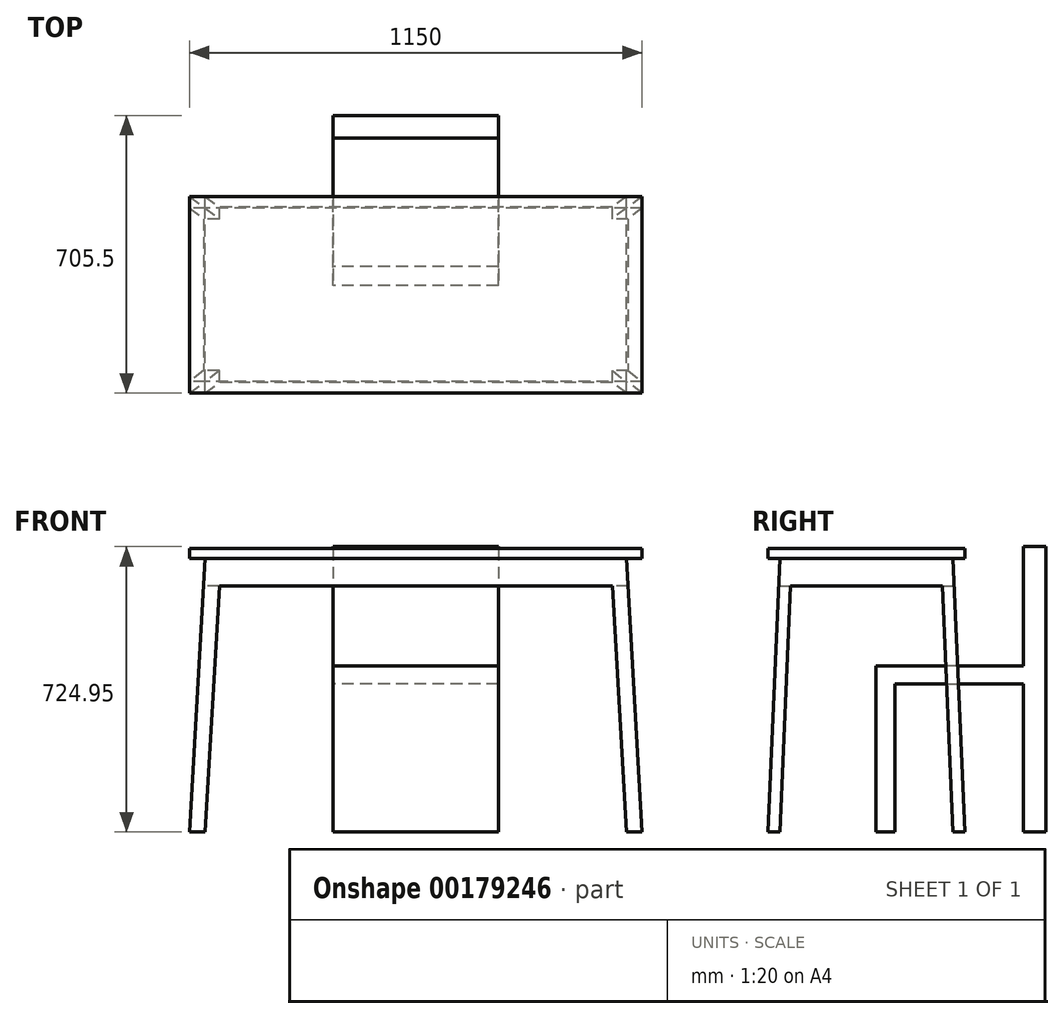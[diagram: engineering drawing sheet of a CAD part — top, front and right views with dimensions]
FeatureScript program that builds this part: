
annotation { "Feature Type Name" : "Feature", "Feature Type Description" : "" }
export const myFeature = defineFeature(function(context is Context, id is Id, definition is map)
    precondition{}
    {
        {
            var Q0;
            Q0=qCreatedBy(makeId("Front.planeOp"),FACE);
            var sketch = newSketch(context, id + "F0", { "sketchPlane" : qUnion([Q0])});
            skLineSegment(sketch, "E0.bottom", {"start": v(-575, 0) * mm, "end": v(575, 0) * mm});
            skLineSegment(sketch, "E0.top", {"start": v(-575, 720) * mm, "end": v(575, 720) * mm});
            skLineSegment(sketch, "E0.left", {"start": v(-575, 0) * mm, "end": v(-575, 720) * mm});
            skLineSegment(sketch, "E0.right", {"start": v(575, 0) * mm, "end": v(575, 720) * mm});
            skSolve(sketch);
        }
        {
            var Q0;
            Q0 = qSketchRegion(id + "F0", true);
            extrude(context, id + "F1", {"entities" : qUnion([Q0]), "depth" : 500 * mm});
        }
        {
            var Q0;
            Q0=makeQuery(id+"F1.opExtrude","CAP_FACE",FACE,{"disambiguationData":[OSD([sQuery(id+"F0.wireOp",EDGE,"E0.bottom"),sQuery(id+"F0.wireOp",EDGE,"E0.top"),sQuery(id+"F0.wireOp",EDGE,"E0.left"),sQuery(id+"F0.wireOp",EDGE,"E0.right")])],"isStart":true});
            var sketch = newSketch(context, id + "F2", { "sketchPlane" : qUnion([Q0])});
            skLineSegment(sketch, "E1", {"start": v(-575, 0) * mm, "end": v(-535, 695) * mm});
            skLineSegment(sketch, "E2", {"start": v(-535, 695) * mm, "end": v(-575, 695) * mm});
            skLineSegment(sketch, "E3", {"start": v(-575, 695) * mm, "end": v(-617.04, 718.64) * mm});
            skLineSegment(sketch, "E4", {"start": v(-617.04, 718.64) * mm, "end": v(-617.04, 757.2) * mm});
            skLineSegment(sketch, "E5", {"start": v(-617.04, 757.2) * mm, "end": v(680.07, 757.2) * mm});
            skLineSegment(sketch, "E6", {"start": v(680.07, 757.2) * mm, "end": v(680.07, 727.9) * mm});
            skLineSegment(sketch, "E7", {"start": v(535, 695) * mm, "end": v(663.8, 695) * mm});
            skLineSegment(sketch, "E8", {"start": v(663.8, 695) * mm, "end": v(680.07, 727.9) * mm});
            skLineSegment(sketch, "E9", {"start": v(575, 0) * mm, "end": v(535, 695) * mm});
            skLineSegment(sketch, "E10", {"start": v(-575, 0) * mm, "end": v(-534.93, 0) * mm});
            skLineSegment(sketch, "E11", {"start": v(-498.96, 625) * mm, "end": v(498.96, 625) * mm});
            skLineSegment(sketch, "E12", {"start": v(534.93, 0) * mm, "end": v(498.96, 625) * mm});
            skLineSegment(sketch, "E13", {"start": v(-534.93, 0) * mm, "end": v(-498.96, 625) * mm});
            skLineSegment(sketch, "E14", {"start": v(534.93, 0) * mm, "end": v(575, 0) * mm});
            skSolve(sketch);
        }
        {
            var Q0;
            {var subQ1=sQuery(id+"F2.wireOp",EDGE,"E3");Q0=makeQuery(id+"F2.imprint","IMPRINT",FACE,{"disambiguationData":[TD([[makeQuery(id+"F2.imprint","IMPRINT",EDGE,{"derivedFrom":subQ1}),-1.0]])]});}
            var Q1;
            {var subQ0=sQuery(id+"F2.wireOp",EDGE,"E1");Q1=makeQuery(id+"F2.imprint","IMPRINT",FACE,{"disambiguationData":[TD([[makeQuery(id+"F2.imprint","IMPRINT",EDGE,{"derivedFrom":subQ0}),1.0]])]});}
            var Q2;
            Q2=makeQuery(id+"F2.imprint","IMPRINT",FACE,{"disambiguationData":[TD([[makeQuery(id+"F2.imprint","IMPRINT",EDGE,{"derivedFrom":sQuery(id+"F2.wireOp",EDGE,"E11")}),-1.0]])]});
            var Q3;
            {var subQ0=sQuery(id+"F2.wireOp",EDGE,"E9");Q3=makeQuery(id+"F2.imprint","IMPRINT",FACE,{"disambiguationData":[TD([[makeQuery(id+"F2.imprint","IMPRINT",EDGE,{"derivedFrom":subQ0}),-1.0]])]});}
            extrude(context, id + "F3", {"entities" : qUnion([Q0, Q1, Q2, Q3]), "operationType" : NewBodyOperationType.REMOVE, "endBound" : BoundingType.THROUGH_ALL, "oppositeDirection" : true, "depth" : 25 * mm});
        }
        {
            var Q0;
            Q0=makeQuery(id+"F1.opExtrude","SWEPT_FACE",FACE,{"disambiguationData":[OSD([sQuery(id+"F0.wireOp",EDGE,"E0.left")])]});
            var sketch = newSketch(context, id + "F4", { "sketchPlane" : qUnion([Q0])});
            skLineSegment(sketch, "E15", {"start": v(0, 0) * mm, "end": v(30, 695) * mm});
            skLineSegment(sketch, "E16", {"start": v(30, 695) * mm, "end": v(-66.16, 695) * mm});
            skLineSegment(sketch, "E17", {"start": v(-66.16, 695) * mm, "end": v(0, 0) * mm});
            skLineSegment(sketch, "E18", {"start": v(500, 0) * mm, "end": v(470, 695) * mm});
            skLineSegment(sketch, "E19", {"start": v(470, 695) * mm, "end": v(521.08, 695) * mm});
            skLineSegment(sketch, "E20", {"start": v(521.08, 695) * mm, "end": v(500, 0) * mm});
            skLineSegment(sketch, "E21", {"start": v(30.03, 0) * mm, "end": v(57, 625) * mm});
            skLineSegment(sketch, "E22", {"start": v(57, 625) * mm, "end": v(443, 625) * mm});
            skLineSegment(sketch, "E23", {"start": v(443, 625) * mm, "end": v(469.97, 0) * mm});
            skLineSegment(sketch, "E24", {"start": v(30.03, 0) * mm, "end": v(469.97, 0) * mm});
            skSolve(sketch);
        }
        {
            var Q0;
            Q0 = qSketchRegion(id + "F4", true);
            extrude(context, id + "F5", {"entities" : qUnion([Q0]), "operationType" : NewBodyOperationType.REMOVE, "endBound" : BoundingType.THROUGH_ALL, "oppositeDirection" : true, "depth" : 25 * mm});
        }
        {
            var Q0;
            Q0=qCreatedBy(makeId("Right.planeOp"),FACE);
            var sketch = newSketch(context, id + "F6", { "sketchPlane" : qUnion([Q0])});
            skLineSegment(sketch, "E25", {"start": v(-177.67, 0) * mm, "end": v(-177.67, 376.62) * mm});
            skLineSegment(sketch, "E26", {"start": v(-177.67, 376.62) * mm, "end": v(148.27, 376.62) * mm});
            skLineSegment(sketch, "E27", {"start": v(148.27, 376.62) * mm, "end": v(148.27, 0) * mm});
            skLineSegment(sketch, "E28", {"start": v(148.27, 0) * mm, "end": v(205.5, 0) * mm});
            skLineSegment(sketch, "E29", {"start": v(205.5, 0) * mm, "end": v(205.5, 724.95) * mm});
            skLineSegment(sketch, "E30", {"start": v(205.5, 724.95) * mm, "end": v(148.27, 724.95) * mm});
            skLineSegment(sketch, "E31", {"start": v(148.27, 724.95) * mm, "end": v(148.27, 421.4) * mm});
            skLineSegment(sketch, "E32", {"start": v(148.27, 421.4) * mm, "end": v(-226.18, 421.4) * mm});
            skLineSegment(sketch, "E33", {"start": v(-226.18, 421.4) * mm, "end": v(-226.18, 0) * mm});
            skLineSegment(sketch, "E34", {"start": v(-226.18, 0) * mm, "end": v(-177.67, 0) * mm});
            skSolve(sketch);
        }
        {
            var Q0;
            Q0 = qSketchRegion(id + "F6", true);
            extrude(context, id + "F7", {"entities" : qUnion([Q0]), "endBound" : BoundingType.SYMMETRIC, "depth" : 420 * mm});
        }
    });
